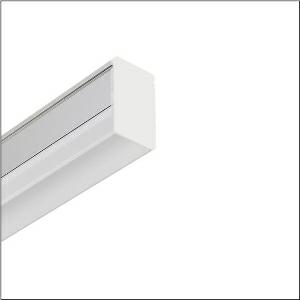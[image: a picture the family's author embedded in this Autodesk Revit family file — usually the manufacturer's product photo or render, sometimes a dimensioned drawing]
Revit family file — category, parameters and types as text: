
# Revit family: siluette_r__41-f_51lp327dm10af_a7bf
name_source: partatom
category: Lighting Fixtures
units: mm (PartAtom-declared; Revit-internal decimal feet)

## family parameters
Cut with Voids When Loaded = No
Host = Face
Light Source = No
Part Type = Normal
Room Calculation Point = No
Round Connector Dimension = Use Diameter
Shared = No

## types (1)
- --- (1 x LED, 1000 lm, 8.3 W, 5000K)
    Apparent Load = 8 VA
    CIE Flux Codes = 39 68 88 89 100
    Color Rendering = 80
    Color Temperature = 5000K
    Default Elevation = 1800 mm
    Description = Siluette® 41-F, batten luminaire, primary optical cover: cover, of PC, frosted, light emission: direct distribution, primary light characteristic: symmetric, installation type: surface-mounted, LED, rated luminous flux: 1.000lm, luminous efficacy: 120lm/W, light colour: 830/840/850, colour temperature: 3000/4000/5000K, control gear: ON/OFF, with terminal, 2-pole, mains connection: 220..240V, AC, 50/60Hz, rated input power: 8.3W, housing, of aluminium, silver, length: 580mm, width: 25mm, height: 44mm, end cap, of PC, white, protection rating (complete): IP20, insulation class (complete): insulation class II (safety insulation), certification: CE, permissible operating ambient temperature: -20..+40°C, packaging unit: 1 piece
    Height = 44 mm
    Lamp = 1 x LED
    Lamp Light Flux = 1000 lm
    Lamp Power = 8.3 W
    Lamp count = 1
    Length = 580 mm
    Luminous efficacy = 120 lm/W
    Manufacturer = Siteco
    ModVariant = No
    Model = 51LP327DM10AF
    Mounting Place = Ceiling
    Mounting Type = Surface mounted
    Number of Poles = 1
    OnlyDefault = Yes
    Power Factor = 1
    Product Name = Siluette® 41-F
    Product group = batten luminaire
    ProductGroupID = 304
    Protection Class = Protection class II
    Protection Degree = IP 20
    RLX_Detail_Level = 1
    RLX_Emergency_Light_Flux = 0 lm
    RLX_Emergency_Type = 0
    RLX_Emergency_Type_DB = No
    RlxData = <blob elided: 27877 chars, md5=a39dd0d9>
    Socket = socket
    Standby Power = 0 W
    System Light Flux = 1000 lm
    System Power = 8 W
    Type Comments = individual setting: colour temperature 5000K
    Type Image = l_1007255.jpg
    URL = http://relux.com
    VarID = @adj_042803
    Voltage = 0 V
    Weight = 0.00 kg
    Width = 25 mm  [stored 0.082021 ft]

note: [stored X ft] marks values corroborated as IEEE doubles in the binary element streams (Revit-internal decimal feet)

## geometry (parser evidence)
native form markers: Blend x4, Sweep x12
no freeform markers — native parametric forms only
